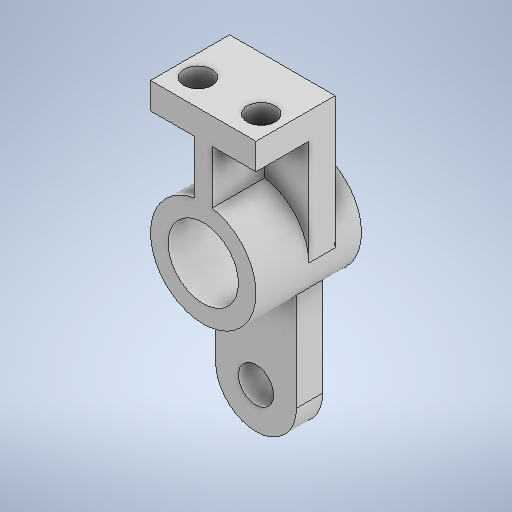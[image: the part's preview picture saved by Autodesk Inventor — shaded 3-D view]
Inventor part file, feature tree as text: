
AUTODESK INVENTOR PART (.ipt)
format: ipt  version: 2025.2 (Build 292293000, 293)  size: 313,344 bytes
history: native  units: in
note: dims shown in document units (in); Inventor stores cm internally (conversion verified against a paired STEP export)
features: sketch x4, extrude x4
ambient origin geometry x8: Origin, YZ Plane, XZ Plane, XY Plane, X Axis, Y Axis, Z Axis, Center Point
bodies: Solid1 (feature_tree)
feature tree (8):
  sketch  "Sketch1"  dims[d0=2.3622in d1=2.9528in]
  extrude  "Extrusion1"  Depth=2.3622in
  extrude  "Extrusion2"  Depth=2.3622in
  extrude  "Extrusion3"  Depth=0.7874in
  sketch  "Sketch2"  dims[d2=2.3622in d3=1.5748in]
  sketch  "Sketch3"  dims[d4=1.811in d5=0.7874in]
  extrude  "Extrusion4"  Depth=0.5906in
  sketch  "Sketch4"  dims[d6=2.9528in d7=0.5906in d9=0.9843in d10=0.5906in d11=0.0in d12=1.7717in d13=0.0in d14=1.7717in d15=0.5906in d16=0.0in d17=0.0in d18=0.6299in d19=0.4724in d20=0.5906in d21=0.5906in d22=0.0in]
